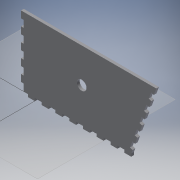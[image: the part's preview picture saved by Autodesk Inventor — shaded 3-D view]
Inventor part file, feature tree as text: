
AUTODESK INVENTOR PART (.ipt)
format: ipt  version: 2019 (Build 230136000, 136)  size: 195,584 bytes
history: native  units: mm
features: reference x9, other x4, extrude x2, sketch x2
ambient origin geometry x8: Origin, YZ Plane, XZ Plane, XY Plane, X Axis, Y Axis, Z Axis, Center Point
bodies: Body1 (feature_tree)
feature tree (17):
  other  "Твердое тело1"
  extrude  "Выдавливание1"  Depth=100.0mm
  extrude  "Выдавливание2"  Depth=12.217305mm
  sketch  "Эскиз1"
  reference  "Ссылка1"
  reference  "Ссылка2"
  reference  "Ссылка3"
  reference  "Ссылка4"
  reference  "Ссылка5"
  reference  "Ссылка6"
  reference  "Ссылка7"
  reference  "Ссылка8"
  reference  "Ссылка9"
  sketch  "Эскиз2"
  parser-record x1  (decoder bookkeeping rows leaked as tree rows — omitted from the tree; the rows remain in map.json)
  other  "kowsh.iam"
  other  "Stenka:1"
note: 1 file-system path scrubbed to <path> (originals preserved in map.json)
